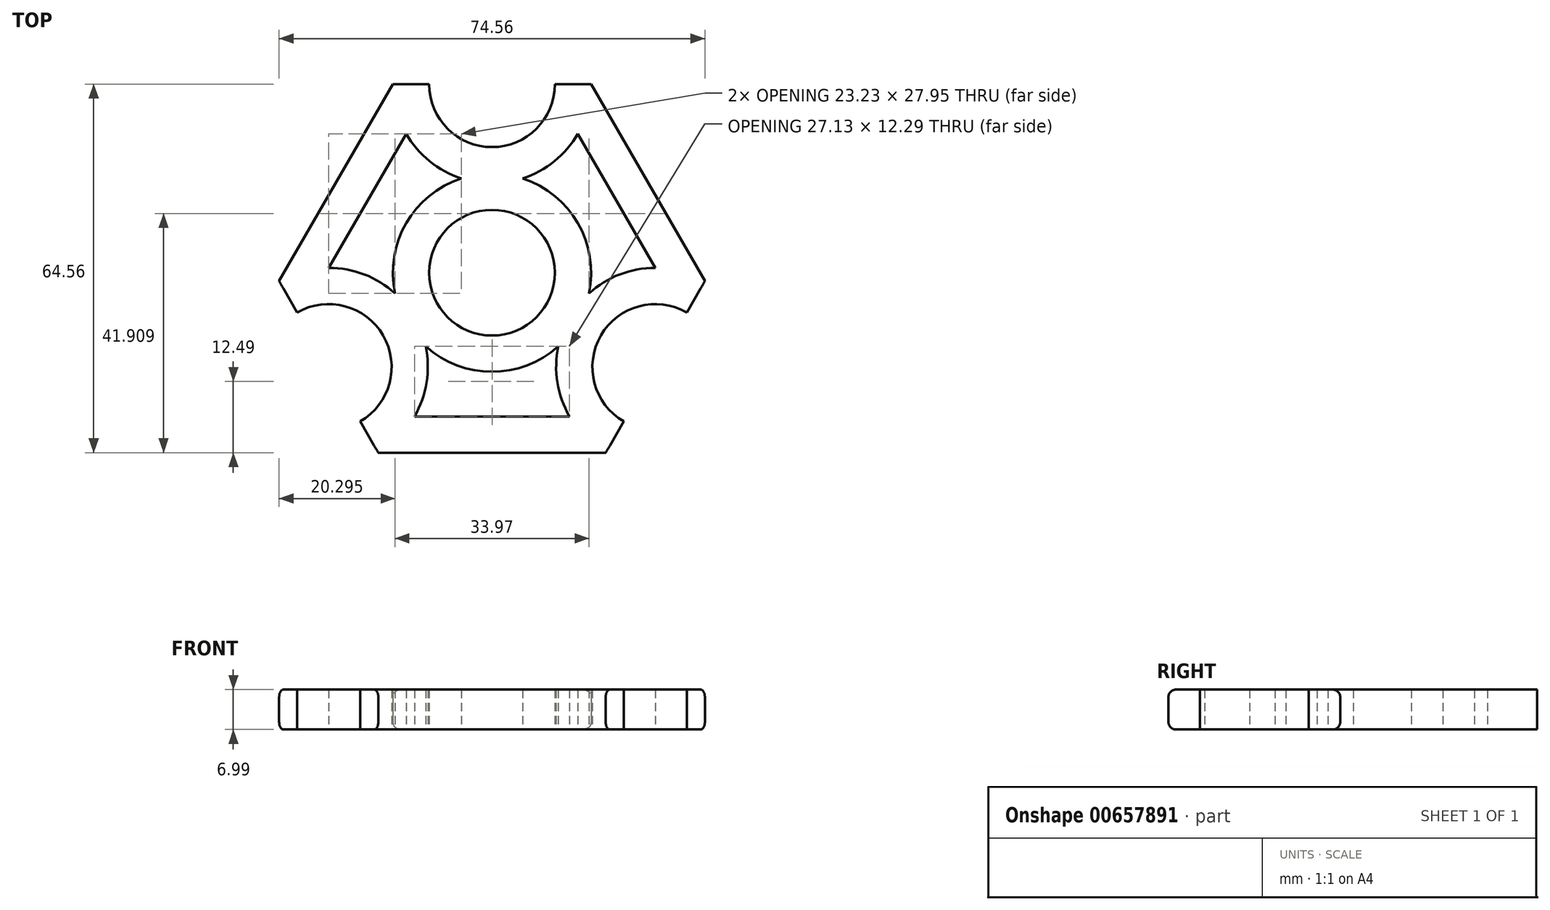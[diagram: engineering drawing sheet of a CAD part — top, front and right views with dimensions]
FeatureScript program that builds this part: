
annotation { "Feature Type Name" : "Feature", "Feature Type Description" : "" }
export const myFeature = defineFeature(function(context is Context, id is Id, definition is map)
    precondition{}
    {
        {
            var Q0;
            Q0=qCreatedBy(makeId("Top.planeOp"),FACE);
            var sketch = newSketch(context, id + "F0", { "sketchPlane" : qUnion([Q0])});
            skCircle(sketch, "E0", {"center": v(0, 0) * mm, "radius": 11.01 * mm});
            skLineSegment(sketch, "E1", {"start": v(0, 0) * mm, "end": v(0, 33.02) * mm});
            skLineSegment(sketch, "E2", {"start": v(0, 0) * mm, "end": v(28.6, -16.5) * mm});
            skLineSegment(sketch, "E3", {"start": v(0, 0) * mm, "end": v(-28.6, -16.51) * mm});
            skCircle(sketch, "E4", {"center": v(0, 33.02) * mm, "radius": 11.01 * mm});
            skCircle(sketch, "E5", {"center": v(28.6, -16.5) * mm, "radius": 11.01 * mm});
            skCircle(sketch, "E6", {"center": v(-28.6, -16.51) * mm, "radius": 11.01 * mm});
            skArc(sketch, "E7.0.startCap", {"start": v(6.35, 0) * mm, "mid": v(0, -6.35) * mm, "end": v(-6.35, 0) * mm});
            skArc(sketch, "E7.0.endCap", {"start": v(-6.35, 33.02) * mm, "mid": v(0, 39.37) * mm, "end": v(6.35, 33.02) * mm});
            skLineSegment(sketch, "E7.0.left", {"start": v(-6.35, 0) * mm, "end": v(-6.35, 33.02) * mm});
            skLineSegment(sketch, "E7.0.right", {"start": v(6.35, 0) * mm, "end": v(6.35, 33.02) * mm});
            skArc(sketch, "E8.0.startCap", {"start": v(-3.18, 5.5) * mm, "mid": v(5.5, 3.18) * mm, "end": v(3.18, -5.5) * mm});
            skArc(sketch, "E8.0.endCap", {"start": v(-25.42, -22) * mm, "mid": v(-34.1, -19.69) * mm, "end": v(-31.77, -11.01) * mm});
            skLineSegment(sketch, "E8.0.left", {"start": v(3.18, -5.5) * mm, "end": v(-25.42, -22) * mm});
            skLineSegment(sketch, "E8.0.right", {"start": v(-3.18, 5.5) * mm, "end": v(-31.77, -11.01) * mm});
            skArc(sketch, "E9.0.startCap", {"start": v(-3.17, -5.5) * mm, "mid": v(-5.5, 3.17) * mm, "end": v(3.17, 5.5) * mm});
            skArc(sketch, "E9.0.endCap", {"start": v(31.77, -11.01) * mm, "mid": v(34.1, -19.68) * mm, "end": v(25.42, -22) * mm});
            skLineSegment(sketch, "E9.0.left", {"start": v(3.17, 5.5) * mm, "end": v(31.77, -11.01) * mm});
            skLineSegment(sketch, "E9.0.right", {"start": v(-3.17, -5.5) * mm, "end": v(25.42, -22) * mm});
            skCircle(sketch, "E10.0", {"center": v(0, 33.02) * mm, "radius": 17.36 * mm});
            skCircle(sketch, "E11.0", {"center": v(28.6, -16.5) * mm, "radius": 17.36 * mm});
            skCircle(sketch, "E12.0", {"center": v(-28.6, -16.51) * mm, "radius": 17.36 * mm});
            skCircle(sketch, "E13.0", {"center": v(0, 0) * mm, "radius": 17.36 * mm});
            skLineSegment(sketch, "E14", {"start": v(0, 33.02) * mm, "end": v(-17.36, 33.02) * mm});
            skLineSegment(sketch, "E15", {"start": v(-28.6, -16.51) * mm, "end": v(-37.28, -1.48) * mm});
            skLineSegment(sketch, "E16", {"start": v(28.6, -16.5) * mm, "end": v(37.28, -1.48) * mm});
            skLineSegment(sketch, "E17", {"start": v(37.28, -1.48) * mm, "end": v(19.92, -31.54) * mm});
            skLineSegment(sketch, "E18", {"start": v(-17.36, 33.02) * mm, "end": v(17.36, 33.02) * mm});
            skLineSegment(sketch, "E19", {"start": v(-37.28, -1.48) * mm, "end": v(-19.92, -31.54) * mm});
            skLineSegment(sketch, "E20", {"start": v(-19.92, -31.54) * mm, "end": v(19.92, -31.54) * mm});
            skLineSegment(sketch, "E21", {"start": v(37.28, -1.48) * mm, "end": v(17.36, 33.02) * mm});
            skLineSegment(sketch, "E22", {"start": v(-17.36, 33.02) * mm, "end": v(-37.28, -1.48) * mm});
            skSolve(sketch);
        }
        {
            var Q0;
            {var subQ0=sQuery(id+"F0.wireOp",EDGE,"E13.0");var subQ1=sQuery(id+"F0.wireOp",EDGE,"E7.0.left");var subQ2=makeQuery(id+"F0.imprint","INTERSECT",VERTEX,{"derivedFrom":[subQ1,subQ0]});Q0=makeQuery(id+"F0.imprint","IMPRINT",FACE,{"disambiguationData":[TD([[makeQuery(id+"F0.imprint","IMPRINT",EDGE,{"disambiguationData":[TD([[subQ2,-1.0]])],"derivedFrom":subQ1}),-1.0]])]});}
            var Q1;
            {var subQ0=sQuery(id+"F0.wireOp",EDGE,"E13.0");var subQ1=sQuery(id+"F0.wireOp",EDGE,"E7.0.right");var subQ2=makeQuery(id+"F0.imprint","INTERSECT",VERTEX,{"derivedFrom":[subQ1,subQ0]});Q1=makeQuery(id+"F0.imprint","IMPRINT",FACE,{"disambiguationData":[TD([[makeQuery(id+"F0.imprint","IMPRINT",EDGE,{"disambiguationData":[TD([[subQ2,-1.0]])],"derivedFrom":subQ1}),1.0]])]});}
            var Q2;
            {var subQ0=sQuery(id+"F0.wireOp",EDGE,"E13.0");var subQ1=sQuery(id+"F0.wireOp",EDGE,"E8.0.left");var subQ2=makeQuery(id+"F0.imprint","INTERSECT",VERTEX,{"derivedFrom":[subQ1,subQ0]});Q2=makeQuery(id+"F0.imprint","IMPRINT",FACE,{"disambiguationData":[TD([[makeQuery(id+"F0.imprint","IMPRINT",EDGE,{"disambiguationData":[TD([[subQ2,-1.0]])],"derivedFrom":subQ1}),-1.0]])]});}
            var Q3;
            {var subQ0=sQuery(id+"F0.wireOp",EDGE,"E13.0");var subQ1=sQuery(id+"F0.wireOp",EDGE,"E8.0.right");var subQ2=makeQuery(id+"F0.imprint","INTERSECT",VERTEX,{"derivedFrom":[subQ1,subQ0]});Q3=makeQuery(id+"F0.imprint","IMPRINT",FACE,{"disambiguationData":[TD([[makeQuery(id+"F0.imprint","IMPRINT",EDGE,{"disambiguationData":[TD([[subQ2,-1.0]])],"derivedFrom":subQ1}),1.0]])]});}
            var Q4;
            {var subQ0=sQuery(id+"F0.wireOp",EDGE,"E13.0");var subQ1=sQuery(id+"F0.wireOp",EDGE,"E9.0.left");var subQ2=makeQuery(id+"F0.imprint","INTERSECT",VERTEX,{"derivedFrom":[subQ1,subQ0]});Q4=makeQuery(id+"F0.imprint","IMPRINT",FACE,{"disambiguationData":[TD([[makeQuery(id+"F0.imprint","IMPRINT",EDGE,{"disambiguationData":[TD([[subQ2,-1.0]])],"derivedFrom":subQ1}),-1.0]])]});}
            var Q5;
            {var subQ0=sQuery(id+"F0.wireOp",EDGE,"E13.0");var subQ1=sQuery(id+"F0.wireOp",EDGE,"E9.0.right");var subQ2=makeQuery(id+"F0.imprint","INTERSECT",VERTEX,{"derivedFrom":[subQ1,subQ0]});Q5=makeQuery(id+"F0.imprint","IMPRINT",FACE,{"disambiguationData":[TD([[makeQuery(id+"F0.imprint","IMPRINT",EDGE,{"disambiguationData":[TD([[subQ2,-1.0]])],"derivedFrom":subQ1}),1.0]])]});}
            var Q6;
            {var subQ0=sQuery(id+"F0.wireOp",EDGE,"E7.0.right");var subQ1=sQuery(id+"F0.wireOp",EDGE,"E0");var subQ2=makeQuery(id+"F0.imprint","INTERSECT",VERTEX,{"derivedFrom":[subQ1,subQ0]});Q6=makeQuery(id+"F0.imprint","IMPRINT",FACE,{"disambiguationData":[TD([[makeQuery(id+"F0.imprint","IMPRINT",EDGE,{"disambiguationData":[TD([[subQ2,1.0]])],"derivedFrom":subQ1}),-1.0]])]});}
            var Q7;
            {var subQ0=sQuery(id+"F0.wireOp",EDGE,"E7.0.left");var subQ1=sQuery(id+"F0.wireOp",EDGE,"E0");var subQ2=makeQuery(id+"F0.imprint","INTERSECT",VERTEX,{"derivedFrom":[subQ1,subQ0]});Q7=makeQuery(id+"F0.imprint","IMPRINT",FACE,{"disambiguationData":[TD([[makeQuery(id+"F0.imprint","IMPRINT",EDGE,{"disambiguationData":[TD([[subQ2,-1.0]])],"derivedFrom":subQ1}),-1.0]])]});}
            var Q8;
            {var subQ0=sQuery(id+"F0.wireOp",EDGE,"E8.0.left");var subQ1=sQuery(id+"F0.wireOp",EDGE,"E0");var subQ2=makeQuery(id+"F0.imprint","INTERSECT",VERTEX,{"derivedFrom":[subQ1,subQ0]});Q8=makeQuery(id+"F0.imprint","IMPRINT",FACE,{"disambiguationData":[TD([[makeQuery(id+"F0.imprint","IMPRINT",EDGE,{"disambiguationData":[TD([[subQ2,-1.0]])],"derivedFrom":subQ1}),-1.0]])]});}
            var Q9;
            {var subQ0=sQuery(id+"F0.wireOp",EDGE,"E7.0.left");var subQ1=sQuery(id+"F0.wireOp",EDGE,"E4");var subQ2=makeQuery(id+"F0.imprint","INTERSECT",VERTEX,{"derivedFrom":[subQ1,subQ0]});Q9=makeQuery(id+"F0.imprint","IMPRINT",FACE,{"disambiguationData":[TD([[makeQuery(id+"F0.imprint","IMPRINT",EDGE,{"disambiguationData":[TD([[subQ2,1.0]])],"derivedFrom":subQ1}),-1.0]])]});}
            var Q10;
            {var subQ0=sQuery(id+"F0.wireOp",EDGE,"E9.0.left");var subQ1=sQuery(id+"F0.wireOp",EDGE,"E5");var subQ2=makeQuery(id+"F0.imprint","INTERSECT",VERTEX,{"derivedFrom":[subQ1,subQ0]});Q10=makeQuery(id+"F0.imprint","IMPRINT",FACE,{"disambiguationData":[TD([[makeQuery(id+"F0.imprint","IMPRINT",EDGE,{"disambiguationData":[TD([[subQ2,1.0]])],"derivedFrom":subQ1}),-1.0]])]});}
            var Q11;
            {var subQ0=sQuery(id+"F0.wireOp",EDGE,"E8.0.right");var subQ1=sQuery(id+"F0.wireOp",EDGE,"E6");var subQ2=makeQuery(id+"F0.imprint","INTERSECT",VERTEX,{"derivedFrom":[subQ1,subQ0]});Q11=makeQuery(id+"F0.imprint","IMPRINT",FACE,{"disambiguationData":[TD([[makeQuery(id+"F0.imprint","IMPRINT",EDGE,{"disambiguationData":[TD([[subQ2,-1.0]])],"derivedFrom":subQ1}),-1.0]])]});}
            var Q12;
            {var subQ5=sQuery(id+"F0.wireOp",EDGE,"E7.0.right");var subQ7=sQuery(id+"F0.wireOp",EDGE,"E0");var subQ8=makeQuery(id+"F0.imprint","INTERSECT",VERTEX,{"derivedFrom":[subQ7,subQ5]});Q12=makeQuery(id+"F0.imprint","IMPRINT",FACE,{"disambiguationData":[TD([[makeQuery(id+"F0.imprint","IMPRINT",EDGE,{"disambiguationData":[TD([[subQ8,-1.0]])],"derivedFrom":subQ7}),-1.0]])]});}
            var Q13;
            {var subQ0=sQuery(id+"F0.wireOp",EDGE,"E1");var subQ1=sQuery(id+"F0.wireOp",EDGE,"E0");var subQ2=makeQuery(id+"F0.imprint","INTERSECT",VERTEX,{"derivedFrom":[subQ1,subQ0]});Q13=makeQuery(id+"F0.imprint","IMPRINT",FACE,{"disambiguationData":[TD([[makeQuery(id+"F0.imprint","IMPRINT",EDGE,{"disambiguationData":[TD([[subQ2,-1.0]])],"derivedFrom":subQ1}),-1.0]])]});}
            var Q14;
            {var subQ5=sQuery(id+"F0.wireOp",EDGE,"E0");var subQ7=sQuery(id+"F0.wireOp",EDGE,"E8.0.right");var subQ9=makeQuery(id+"F0.imprint","INTERSECT",VERTEX,{"derivedFrom":[subQ5,subQ7]});Q14=makeQuery(id+"F0.imprint","IMPRINT",FACE,{"disambiguationData":[TD([[makeQuery(id+"F0.imprint","IMPRINT",EDGE,{"disambiguationData":[TD([[subQ9,-1.0]])],"derivedFrom":subQ5}),-1.0]])]});}
            var Q15;
            {var subQ5=sQuery(id+"F0.wireOp",EDGE,"E9.0.right");var subQ7=sQuery(id+"F0.wireOp",EDGE,"E0");var subQ8=makeQuery(id+"F0.imprint","INTERSECT",VERTEX,{"derivedFrom":[subQ7,subQ5]});Q15=makeQuery(id+"F0.imprint","IMPRINT",FACE,{"disambiguationData":[TD([[makeQuery(id+"F0.imprint","IMPRINT",EDGE,{"disambiguationData":[TD([[subQ8,-1.0]])],"derivedFrom":subQ7}),-1.0]])]});}
            var Q16;
            {var subQ5=sQuery(id+"F0.wireOp",EDGE,"E9.0.left");var subQ7=sQuery(id+"F0.wireOp",EDGE,"E0");var subQ8=makeQuery(id+"F0.imprint","INTERSECT",VERTEX,{"derivedFrom":[subQ7,subQ5]});Q16=makeQuery(id+"F0.imprint","IMPRINT",FACE,{"disambiguationData":[TD([[makeQuery(id+"F0.imprint","IMPRINT",EDGE,{"disambiguationData":[TD([[subQ8,1.0]])],"derivedFrom":subQ7}),-1.0]])]});}
            var Q17;
            {var subQ5=sQuery(id+"F0.wireOp",EDGE,"E4");var subQ7=sQuery(id+"F0.wireOp",EDGE,"E1");var subQ8=makeQuery(id+"F0.imprint","INTERSECT",VERTEX,{"derivedFrom":[subQ7,subQ5]});Q17=makeQuery(id+"F0.imprint","IMPRINT",FACE,{"disambiguationData":[TD([[makeQuery(id+"F0.imprint","IMPRINT",EDGE,{"disambiguationData":[TD([[subQ8,1.0]])],"derivedFrom":subQ7}),1.0]])]});}
            var Q18;
            {var subQ5=sQuery(id+"F0.wireOp",EDGE,"E4");var subQ7=sQuery(id+"F0.wireOp",EDGE,"E1");var subQ8=makeQuery(id+"F0.imprint","INTERSECT",VERTEX,{"derivedFrom":[subQ7,subQ5]});Q18=makeQuery(id+"F0.imprint","IMPRINT",FACE,{"disambiguationData":[TD([[makeQuery(id+"F0.imprint","IMPRINT",EDGE,{"disambiguationData":[TD([[subQ8,1.0]])],"derivedFrom":subQ7}),-1.0]])]});}
            var Q19;
            {var subQ5=sQuery(id+"F0.wireOp",EDGE,"E5");var subQ7=sQuery(id+"F0.wireOp",EDGE,"E2");var subQ8=makeQuery(id+"F0.imprint","INTERSECT",VERTEX,{"derivedFrom":[subQ7,subQ5]});Q19=makeQuery(id+"F0.imprint","IMPRINT",FACE,{"disambiguationData":[TD([[makeQuery(id+"F0.imprint","IMPRINT",EDGE,{"disambiguationData":[TD([[subQ8,1.0]])],"derivedFrom":subQ7}),-1.0]])]});}
            var Q20;
            {var subQ5=sQuery(id+"F0.wireOp",EDGE,"E6");var subQ7=sQuery(id+"F0.wireOp",EDGE,"E3");var subQ8=makeQuery(id+"F0.imprint","INTERSECT",VERTEX,{"derivedFrom":[subQ7,subQ5]});Q20=makeQuery(id+"F0.imprint","IMPRINT",FACE,{"disambiguationData":[TD([[makeQuery(id+"F0.imprint","IMPRINT",EDGE,{"disambiguationData":[TD([[subQ8,1.0]])],"derivedFrom":subQ7}),-1.0]])]});}
            var Q21;
            {var subQ0=sQuery(id+"F0.wireOp",EDGE,"E10.0");var subQ1=sQuery(id+"F0.wireOp",EDGE,"E1");var subQ2=makeQuery(id+"F0.imprint","INTERSECT",VERTEX,{"derivedFrom":[subQ1,subQ0]});Q21=makeQuery(id+"F0.imprint","IMPRINT",FACE,{"disambiguationData":[TD([[makeQuery(id+"F0.imprint","IMPRINT",EDGE,{"disambiguationData":[TD([[subQ2,-1.0]])],"derivedFrom":subQ1}),-1.0]])]});}
            var Q22;
            {var subQ0=sQuery(id+"F0.wireOp",EDGE,"E10.0");var subQ1=sQuery(id+"F0.wireOp",EDGE,"E1");var subQ2=makeQuery(id+"F0.imprint","INTERSECT",VERTEX,{"derivedFrom":[subQ1,subQ0]});Q22=makeQuery(id+"F0.imprint","IMPRINT",FACE,{"disambiguationData":[TD([[makeQuery(id+"F0.imprint","IMPRINT",EDGE,{"disambiguationData":[TD([[subQ2,-1.0]])],"derivedFrom":subQ1}),1.0]])]});}
            var Q23;
            {var subQ0=sQuery(id+"F0.wireOp",EDGE,"E11.0");var subQ1=sQuery(id+"F0.wireOp",EDGE,"E2");var subQ2=makeQuery(id+"F0.imprint","INTERSECT",VERTEX,{"derivedFrom":[subQ1,subQ0]});Q23=makeQuery(id+"F0.imprint","IMPRINT",FACE,{"disambiguationData":[TD([[makeQuery(id+"F0.imprint","IMPRINT",EDGE,{"disambiguationData":[TD([[subQ2,-1.0]])],"derivedFrom":subQ1}),-1.0]])]});}
            var Q24;
            {var subQ0=sQuery(id+"F0.wireOp",EDGE,"E12.0");var subQ1=sQuery(id+"F0.wireOp",EDGE,"E3");var subQ2=makeQuery(id+"F0.imprint","INTERSECT",VERTEX,{"derivedFrom":[subQ1,subQ0]});Q24=makeQuery(id+"F0.imprint","IMPRINT",FACE,{"disambiguationData":[TD([[makeQuery(id+"F0.imprint","IMPRINT",EDGE,{"disambiguationData":[TD([[subQ2,-1.0]])],"derivedFrom":subQ1}),-1.0]])]});}
            var Q25;
            {var subQ1=sQuery(id+"F0.wireOp",EDGE,"E3");var subQ7=sQuery(id+"F0.wireOp",EDGE,"E0");var subQ9=makeQuery(id+"F0.imprint","INTERSECT",VERTEX,{"derivedFrom":[subQ7,subQ1]});Q25=makeQuery(id+"F0.imprint","IMPRINT",FACE,{"disambiguationData":[TD([[makeQuery(id+"F0.imprint","IMPRINT",EDGE,{"disambiguationData":[TD([[subQ9,-1.0]])],"derivedFrom":subQ7}),-1.0]])]});}
            var Q26;
            {var subQ5=sQuery(id+"F0.wireOp",EDGE,"E6");var subQ7=sQuery(id+"F0.wireOp",EDGE,"E3");var subQ8=makeQuery(id+"F0.imprint","INTERSECT",VERTEX,{"derivedFrom":[subQ7,subQ5]});Q26=makeQuery(id+"F0.imprint","IMPRINT",FACE,{"disambiguationData":[TD([[makeQuery(id+"F0.imprint","IMPRINT",EDGE,{"disambiguationData":[TD([[subQ8,1.0]])],"derivedFrom":subQ7}),1.0]])]});}
            var Q27;
            {var subQ0=sQuery(id+"F0.wireOp",EDGE,"E12.0");var subQ1=sQuery(id+"F0.wireOp",EDGE,"E3");var subQ2=makeQuery(id+"F0.imprint","INTERSECT",VERTEX,{"derivedFrom":[subQ1,subQ0]});Q27=makeQuery(id+"F0.imprint","IMPRINT",FACE,{"disambiguationData":[TD([[makeQuery(id+"F0.imprint","IMPRINT",EDGE,{"disambiguationData":[TD([[subQ2,-1.0]])],"derivedFrom":subQ1}),1.0]])]});}
            var Q28;
            {var subQ0=sQuery(id+"F0.wireOp",EDGE,"E11.0");var subQ1=sQuery(id+"F0.wireOp",EDGE,"E2");var subQ2=makeQuery(id+"F0.imprint","INTERSECT",VERTEX,{"derivedFrom":[subQ1,subQ0]});Q28=makeQuery(id+"F0.imprint","IMPRINT",FACE,{"disambiguationData":[TD([[makeQuery(id+"F0.imprint","IMPRINT",EDGE,{"disambiguationData":[TD([[subQ2,-1.0]])],"derivedFrom":subQ1}),1.0]])]});}
            var Q29;
            {var subQ5=sQuery(id+"F0.wireOp",EDGE,"E2");var subQ7=sQuery(id+"F0.wireOp",EDGE,"E5");var subQ8=makeQuery(id+"F0.imprint","INTERSECT",VERTEX,{"derivedFrom":[subQ5,subQ7]});Q29=makeQuery(id+"F0.imprint","IMPRINT",FACE,{"disambiguationData":[TD([[makeQuery(id+"F0.imprint","IMPRINT",EDGE,{"disambiguationData":[TD([[subQ8,1.0]])],"derivedFrom":subQ5}),1.0]])]});}
            var Q30;
            {var subQ0=sQuery(id+"F0.wireOp",EDGE,"E18");var subQ1=sQuery(id+"F0.wireOp",EDGE,"E4");var subQ2=makeQuery(id+"F0.imprint","INTERSECT",VERTEX,{"disambiguationData":[OD(1.0)],"derivedFrom":[subQ1,subQ0]});Q30=makeQuery(id+"F0.imprint","IMPRINT",FACE,{"disambiguationData":[TD([[makeQuery(id+"F0.imprint","IMPRINT",EDGE,{"disambiguationData":[TD([[subQ2,1.0]])],"derivedFrom":subQ1}),-1.0]])]});}
            var Q31;
            {var subQ0=sQuery(id+"F0.wireOp",EDGE,"E18");var subQ1=sQuery(id+"F0.wireOp",EDGE,"E4");var subQ2=makeQuery(id+"F0.imprint","INTERSECT",VERTEX,{"disambiguationData":[OD(0.0)],"derivedFrom":[subQ1,subQ0]});Q31=makeQuery(id+"F0.imprint","IMPRINT",FACE,{"disambiguationData":[TD([[makeQuery(id+"F0.imprint","IMPRINT",EDGE,{"disambiguationData":[TD([[subQ2,1.0]])],"derivedFrom":subQ1}),-1.0]])]});}
            var Q32;
            {var subQ0=sQuery(id+"F0.wireOp",EDGE,"E17");var subQ1=sQuery(id+"F0.wireOp",EDGE,"E5");var subQ2=makeQuery(id+"F0.imprint","INTERSECT",VERTEX,{"disambiguationData":[OD(0.0)],"derivedFrom":[subQ1,subQ0]});Q32=makeQuery(id+"F0.imprint","IMPRINT",FACE,{"disambiguationData":[TD([[makeQuery(id+"F0.imprint","IMPRINT",EDGE,{"disambiguationData":[TD([[subQ2,1.0]])],"derivedFrom":subQ1}),-1.0]])]});}
            var Q33;
            {var subQ0=sQuery(id+"F0.wireOp",EDGE,"E9.0.right");var subQ1=sQuery(id+"F0.wireOp",EDGE,"E5");var subQ2=makeQuery(id+"F0.imprint","INTERSECT",VERTEX,{"derivedFrom":[subQ1,subQ0]});Q33=makeQuery(id+"F0.imprint","IMPRINT",FACE,{"disambiguationData":[TD([[makeQuery(id+"F0.imprint","IMPRINT",EDGE,{"disambiguationData":[TD([[subQ2,-1.0]])],"derivedFrom":subQ1}),-1.0]])]});}
            var Q34;
            {var subQ0=sQuery(id+"F0.wireOp",EDGE,"E19");var subQ1=sQuery(id+"F0.wireOp",EDGE,"E6");var subQ2=makeQuery(id+"F0.imprint","INTERSECT",VERTEX,{"disambiguationData":[OD(0.0)],"derivedFrom":[subQ1,subQ0]});Q34=makeQuery(id+"F0.imprint","IMPRINT",FACE,{"disambiguationData":[TD([[makeQuery(id+"F0.imprint","IMPRINT",EDGE,{"disambiguationData":[TD([[subQ2,-1.0]])],"derivedFrom":subQ1}),-1.0]])]});}
            var Q35;
            {var subQ0=sQuery(id+"F0.wireOp",EDGE,"E19");var subQ1=sQuery(id+"F0.wireOp",EDGE,"E6");var subQ2=makeQuery(id+"F0.imprint","INTERSECT",VERTEX,{"disambiguationData":[OD(1.0)],"derivedFrom":[subQ1,subQ0]});Q35=makeQuery(id+"F0.imprint","IMPRINT",FACE,{"disambiguationData":[TD([[makeQuery(id+"F0.imprint","IMPRINT",EDGE,{"disambiguationData":[TD([[subQ2,-1.0]])],"derivedFrom":subQ1}),-1.0]])]});}
            var Q36;
            {var subQ0=sQuery(id+"F0.wireOp",EDGE,"E20");Q36=makeQuery(id+"F0.imprint","IMPRINT",FACE,{"disambiguationData":[TD([[makeQuery(id+"F0.imprint","IMPRINT",EDGE,{"derivedFrom":subQ0}),1.0]])]});}
            var Q37;
            {var subQ0=sQuery(id+"F0.wireOp",EDGE,"E21");Q37=makeQuery(id+"F0.imprint","IMPRINT",FACE,{"disambiguationData":[TD([[makeQuery(id+"F0.imprint","IMPRINT",EDGE,{"derivedFrom":subQ0}),1.0]])]});}
            var Q38;
            {var subQ0=sQuery(id+"F0.wireOp",EDGE,"E22");Q38=makeQuery(id+"F0.imprint","IMPRINT",FACE,{"disambiguationData":[TD([[makeQuery(id+"F0.imprint","IMPRINT",EDGE,{"derivedFrom":subQ0}),1.0]])]});}
            extrude(context, id + "F1", {"entities" : qUnion([Q0, Q1, Q2, Q3, Q4, Q5, Q6, Q7, Q8, Q9, Q10, Q11, Q12, Q13, Q14, Q15, Q16, Q17, Q18, Q19, Q20, Q21, Q22, Q23, Q24, Q25, Q26, Q27, Q28, Q29, Q30, Q31, Q32, Q33, Q34, Q35, Q36, Q37, Q38]), "depth" : 7 * mm, "offsetDistance" : 25.4 * mm});
        }
        {
            var Q0;
            Q0=makeQuery(id+"F1.opExtrude","CAP_EDGE",EDGE,{"disambiguationData":[OSD([sQuery(id+"F0.wireOp",EDGE,"E22")])],"isStart":false});
            var Q1;
            Q1=makeQuery(id+"F1.opExtrude","CAP_EDGE",EDGE,{"disambiguationData":[OSD([sQuery(id+"F0.wireOp",EDGE,"E10.0")])],"isStart":true});
            var Q2;
            Q2=makeQuery(id+"F1.opExtrude","CAP_EDGE",EDGE,{"disambiguationData":[OSD([sQuery(id+"F0.wireOp",EDGE,"E21")])],"isStart":true});
            var Q3;
            Q3=makeQuery(id+"F1.opExtrude","CAP_EDGE",EDGE,{"disambiguationData":[OSD([sQuery(id+"F0.wireOp",EDGE,"E20")])],"isStart":true});
            var Q4;
            Q4=makeQuery(id+"F1.opExtrude","CAP_EDGE",EDGE,{"disambiguationData":[OSD([sQuery(id+"F0.wireOp",EDGE,"E12.0")])],"isStart":true});
            var Q5;
            Q5=makeQuery(id+"F1.opExtrude","CAP_EDGE",EDGE,{"disambiguationData":[OSD([sQuery(id+"F0.wireOp",EDGE,"E11.0")])],"isStart":true});
            var Q6;
            Q6=makeQuery(id+"F1.opExtrude","CAP_EDGE",EDGE,{"disambiguationData":[OSD([sQuery(id+"F0.wireOp",EDGE,"E22")])],"isStart":true});
            var Q7;
            Q7=makeQuery(id+"F1.opExtrude","CAP_EDGE",EDGE,{"disambiguationData":[OSD([sQuery(id+"F0.wireOp",EDGE,"E10.0")])],"isStart":false});
            var Q8;
            Q8=makeQuery(id+"F1.opExtrude","CAP_EDGE",EDGE,{"disambiguationData":[OSD([sQuery(id+"F0.wireOp",EDGE,"E21")])],"isStart":false});
            var Q9;
            Q9=makeQuery(id+"F1.opExtrude","CAP_EDGE",EDGE,{"disambiguationData":[OSD([sQuery(id+"F0.wireOp",EDGE,"E11.0")])],"isStart":false});
            var Q10;
            Q10=makeQuery(id+"F1.opExtrude","CAP_EDGE",EDGE,{"disambiguationData":[OSD([sQuery(id+"F0.wireOp",EDGE,"E20")])],"isStart":false});
            var Q11;
            Q11=makeQuery(id+"F1.opExtrude","CAP_EDGE",EDGE,{"disambiguationData":[OSD([sQuery(id+"F0.wireOp",EDGE,"E12.0")])],"isStart":false});
            fillet(context, id + "F2", {"entities" : qUnion([Q0, Q1, Q2, Q3, Q4, Q5, Q6, Q7, Q8, Q9, Q10, Q11]), "radius" : 1.27 * mm, "tangentPropagation" : true, "allowEdgeOverflow" : false});
        }
        {
            var Q0;
            Q0=makeQuery(id+"F1.opExtrude","CAP_FACE",FACE,{"disambiguationData":[OSD([sQuery(id+"F0.wireOp",EDGE,"E0"),sQuery(id+"F0.wireOp",EDGE,"E4"),sQuery(id+"F0.wireOp",EDGE,"E5"),sQuery(id+"F0.wireOp",EDGE,"E6"),sQuery(id+"F0.wireOp",EDGE,"E10.0"),sQuery(id+"F0.wireOp",EDGE,"E11.0"),sQuery(id+"F0.wireOp",EDGE,"E12.0"),sQuery(id+"F0.wireOp",EDGE,"E20"),sQuery(id+"F0.wireOp",EDGE,"E21"),sQuery(id+"F0.wireOp",EDGE,"E22")])],"isStart":false});
            var Q1;
            Q1=makeQuery(id+"F1.opExtrude","CAP_FACE",FACE,{"disambiguationData":[OSD([sQuery(id+"F0.wireOp",EDGE,"E0"),sQuery(id+"F0.wireOp",EDGE,"E4"),sQuery(id+"F0.wireOp",EDGE,"E5"),sQuery(id+"F0.wireOp",EDGE,"E6"),sQuery(id+"F0.wireOp",EDGE,"E10.0"),sQuery(id+"F0.wireOp",EDGE,"E11.0"),sQuery(id+"F0.wireOp",EDGE,"E12.0"),sQuery(id+"F0.wireOp",EDGE,"E20"),sQuery(id+"F0.wireOp",EDGE,"E21"),sQuery(id+"F0.wireOp",EDGE,"E22")])],"isStart":true});
            shell(context, id + "F3", {"entities" : qUnion([Q0, Q1]), "thickness" : 6.35 * mm});
        }
    });
